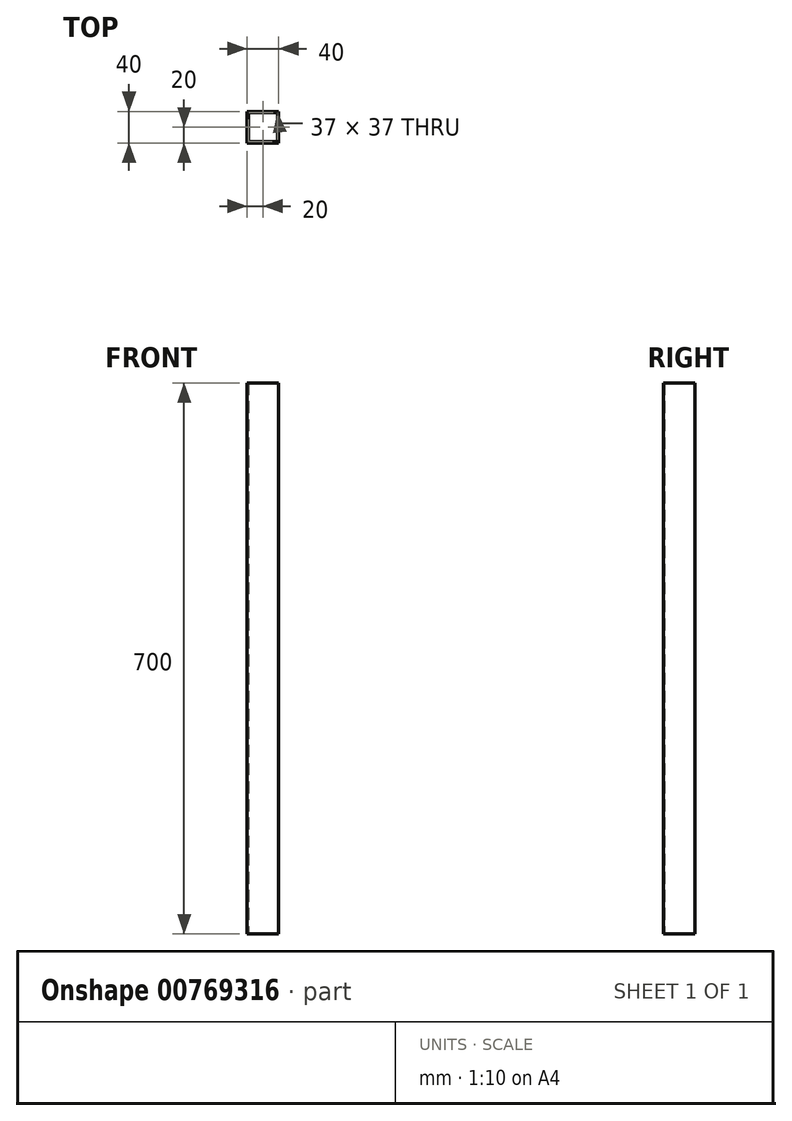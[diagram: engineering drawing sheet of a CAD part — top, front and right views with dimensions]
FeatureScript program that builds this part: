
annotation { "Feature Type Name" : "Feature", "Feature Type Description" : "" }
export const myFeature = defineFeature(function(context is Context, id is Id, definition is map)
    precondition{}
    {
        {
            var Q0;
            Q0=qCreatedBy(makeId("Top.planeOp"),FACE);
            var sketch = newSketch(context, id + "F0", { "sketchPlane" : qUnion([Q0])});
            skLineSegment(sketch, "E0.bottom", {"start": v(20, 20) * mm, "end": v(-20, 20) * mm});
            skLineSegment(sketch, "E0.top", {"start": v(20, -20) * mm, "end": v(-20, -20) * mm});
            skLineSegment(sketch, "E0.left", {"start": v(20, 20) * mm, "end": v(20, -20) * mm});
            skLineSegment(sketch, "E0.right", {"start": v(-20, 20) * mm, "end": v(-20, -20) * mm});
            skPoint(sketch, "E0.middle", {"position": v(0, 0) * mm});
            skLineSegment(sketch, "E1.bottom", {"start": v(18.5, 18.5) * mm, "end": v(-18.5, 18.5) * mm});
            skLineSegment(sketch, "E1.top", {"start": v(18.5, -18.5) * mm, "end": v(-18.5, -18.5) * mm});
            skLineSegment(sketch, "E1.left", {"start": v(18.5, 18.5) * mm, "end": v(18.5, -18.5) * mm});
            skLineSegment(sketch, "E1.right", {"start": v(-18.5, 18.5) * mm, "end": v(-18.5, -18.5) * mm});
            skSolve(sketch);
        }
        {
            var Q0;
            Q0=makeQuery(id+"F0.imprint","IMPRINT",FACE,{"disambiguationData":[TD([[makeQuery(id+"F0.imprint","IMPRINT",EDGE,{"derivedFrom":sQuery(id+"F0.wireOp",EDGE,"E0.bottom")}),1.0]])]});
            extrude(context, id + "F1", {"entities" : qUnion([Q0]), "depth" : 700 * mm, "offsetDistance" : 25 * mm});
        }
    });
